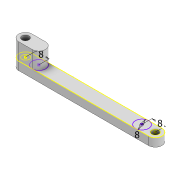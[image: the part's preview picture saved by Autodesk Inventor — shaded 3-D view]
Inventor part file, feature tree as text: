
AUTODESK INVENTOR PART (.ipt)
format: ipt  version: 2022 (Build 260153000, 153)  size: 116,736 bytes
history: native  units: mm
features: extrude x2, sketch x2, projected_geometry x1
ambient origin geometry x8: Origin, YZ Plane, XZ Plane, XY Plane, X Axis, Y Axis, Z Axis, Center Point
bodies: Solid1 (feature_tree)
feature tree (5):
  extrude  "Extrusion1"  Depth=8.0mm
  sketch  "Sketch2"  dims[d2=4.2mm d4=5.0mm d5=0.0mm d10=4.2mm d11=8.0mm d12=8.0mm d13=8.0mm d14=10.0mm d15=0.0mm]
  extrude  "Extrusion2"  Depth=5.0mm TaperAngle=0.0deg
  sketch  "Sketch1"  dims[d0=77.789mm d1=8.0mm]
  projected_geometry  "Projected Loop1"
